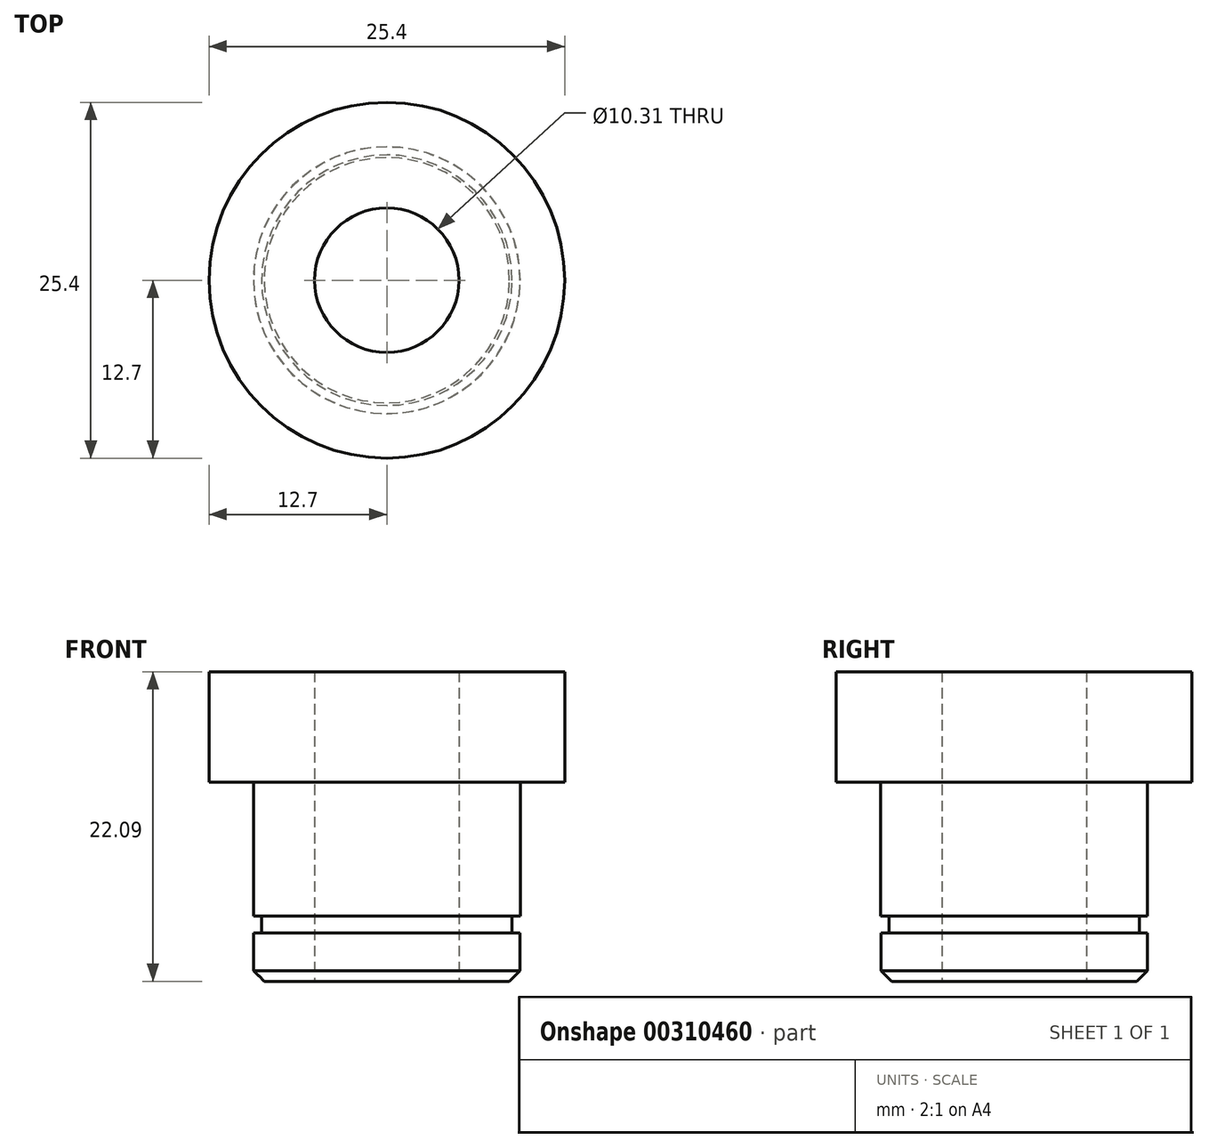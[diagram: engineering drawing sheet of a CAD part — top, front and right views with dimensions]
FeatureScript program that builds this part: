
annotation { "Feature Type Name" : "Feature", "Feature Type Description" : "" }
export const myFeature = defineFeature(function(context is Context, id is Id, definition is map)
    precondition{}
    {
        {
            var Q0;
            Q0=qCreatedBy(makeId("Top.planeOp"),FACE);
            var sketch = newSketch(context, id + "F0", { "sketchPlane" : qUnion([Q0])});
            skCircle(sketch, "E0", {"center": v(0, 0) * mm, "radius": 12.7 * mm});
            skSolve(sketch);
        }
        {
            var Q0;
            Q0=qSketchRegion(id+"F0",true);
            extrude(context, id + "F1", {"entities" : qUnion([Q0]), "depth" : 7.87 * mm});
        }
        {
            var Q0;
            Q0=qCreatedBy(makeId("Top.planeOp"),FACE);
            var sketch = newSketch(context, id + "F2", { "sketchPlane" : qUnion([Q0])});
            skCircle(sketch, "E1", {"center": v(0, 0) * mm, "radius": 9.53 * mm});
            skSolve(sketch);
        }
        {
            var Q0;
            Q0=qSketchRegion(id+"F2",true);
            extrude(context, id + "F3", {"entities" : qUnion([Q0]), "operationType" : NewBodyOperationType.ADD, "oppositeDirection" : true, "depth" : 9.58 * mm});
        }
        {
            var Q0;
            Q0=makeQuery(id+"F3.opExtrude","CAP_FACE",FACE,{"disambiguationData":[OSD([sQuery(id+"F2.wireOp",EDGE,"E1")])],"isStart":false});
            var sketch = newSketch(context, id + "F4", { "sketchPlane" : qUnion([Q0])});
            skCircle(sketch, "E2", {"center": v(0, 0) * mm, "radius": 8.94 * mm});
            skSolve(sketch);
        }
        {
            var Q0;
            Q0=qSketchRegion(id+"F4",true);
            extrude(context, id + "F5", {"entities" : qUnion([Q0]), "operationType" : NewBodyOperationType.ADD, "depth" : 1.2 * mm});
        }
        {
            var Q0;
            Q0=makeQuery(id+"F5.opExtrude","CAP_FACE",FACE,{"disambiguationData":[OSD([sQuery(id+"F4.wireOp",EDGE,"E2")])],"isStart":false});
            var sketch = newSketch(context, id + "F6", { "sketchPlane" : qUnion([Q0])});
            skCircle(sketch, "E3", {"center": v(0, 0) * mm, "radius": 9.51 * mm});
            skSolve(sketch);
        }
        {
            var Q0;
            Q0=qSketchRegion(id+"F6",true);
            extrude(context, id + "F7", {"entities" : qUnion([Q0]), "operationType" : NewBodyOperationType.ADD, "depth" : 3.45 * mm});
        }
        {
            var Q0;
            Q0=makeQuery(id+"F7.opExtrude","CAP_EDGE",EDGE,{"disambiguationData":[OSD([sQuery(id+"F6.wireOp",EDGE,"E3")])],"isStart":false});
            chamfer(context, id + "F8", {"entities" : qUnion([Q0]), "width" : 0.76 * mm, "tangentPropagation" : true});
        }
        {
            var Q0;
            Q0=makeQuery(id+"F7.opExtrude","CAP_FACE",FACE,{"disambiguationData":[OSD([sQuery(id+"F6.wireOp",EDGE,"E3")])],"isStart":false});
            var sketch = newSketch(context, id + "F9", { "sketchPlane" : qUnion([Q0])});
            skPoint(sketch, "E4", {"position": v(0, 0) * mm});
            skSolve(sketch);
        }
        {
            var Q0;
            Q0=sQuery(id+"F9.wireOp",VERTEX,"E4");
            var Q1;
            Q1=makeQuery(id+"F1.opExtrude","SWEPT_BODY",BODY,{"disambiguationData":[OSD([sQuery(id+"F0.wireOp",EDGE,"E0")])]});
            hole(context, id + "F10", {"style" : HoleStyle.SIMPLE, "endStyle" : HoleEndStyle.THROUGH, "holeDiameter" : 10.3 * mm, "tappedDepth" : 24.13 * mm, "tapClearance" : 3, "startFromSketch" : true, "locations" : qUnion([Q0]), "scope" : qUnion([Q1])});
        }
    });
